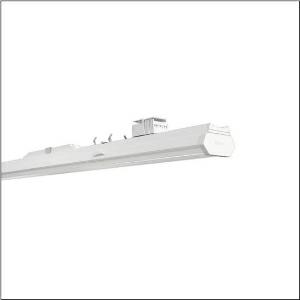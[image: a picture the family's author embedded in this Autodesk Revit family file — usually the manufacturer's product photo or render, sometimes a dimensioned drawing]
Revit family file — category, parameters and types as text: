
# Revit family: licross_r__21_protected_mo_52td1b7n48xg_600d
name_source: partatom
category: Lighting Fixtures
units: mm (PartAtom-declared; Revit-internal decimal feet)

## family parameters
Cut with Voids When Loaded = No
Host = Face
Light Source = No
Part Type = Normal
Room Calculation Point = No
Round Connector Dimension = Use Diameter
Shared = No

## types (1)
- Licross® 21 Protected MO (1 x LED, 8090 lm, 47.9 W, 4000K)
    Apparent Load = 48 VA
    CIE Flux Codes = 54 82 95 97 100
    Color Rendering = 80
    Color Temperature = 4000K
    Default Elevation = 1800 mm
    Description = Licross® 21 Protected MO, luminaire insert, of sheet steel, galvanised, coil coated, white, length: 1.500mm, width: 90mm, height: 103mm, LED rated luminous flux: 8.090lm, light colour: 840, control gear: ON/OFF, with plug, 3-pole, with phase selection, mains connection: 220..240V, AC, 50/60Hz, rated input power: 48W, halogen-free wiring, primary optical cover: cover, of PMMA, light emission: direct distribution, primary light characteristic: symmetric, protection rating (complete): IP54, insulation class (complete): insulation class I (protective earthing), certification: CE, ENEC, VDE, UKCA, protection symbol: D if used in an environment with non-conductive dust loads with corresponding accessories, impact resistance: IK06, permissible ambient temperature for indoor applications: -35..+45°C, corresponds to IFS (International Featured Standards) requirements for safety and quality in the food industry, reducing of maximum allowable ambient temperature of 5°C with ceiling mounting, LABS conformity tested according to VDMA 24364:2018-05, packaging unit: 1 piece
    Height = 92 mm
    Lamp = 1 x LED
    Lamp Light Flux = 8090 lm
    Lamp Power = 47.9 W
    Lamp count = 1
    Length = 1500 mm
    Luminous efficacy = 169 lm/W
    Manufacturer = Siteco
    ModVariant = No
    Model = 52TD1B7N48XG
    Mounting Place = Ceiling
    Mounting Type = Pendant
    Number of Poles = 1
    OnlyDefault = Yes
    Power Factor = 1
    Product Name = Licross® 21 Protected MO
    Product group = luminaire insert
    ProductGroupID = 902
    Protection Class = Protection class I
    Protection Degree = IP 54
    RLX_Detail_Level = 1
    RLX_Emergency_Light_Flux = 0 lm
    RLX_Emergency_Type = 0
    RLX_Emergency_Type_DB = No
    RlxData = <blob elided: 20613 chars, md5=c6c669b1>
    Socket = socket
    Standby Power = 0 W
    System Light Flux = 8090 lm
    System Power = 48 W
    Type Comments = Product without accessories
    Type Image = l_1256148.jpg
    URL = http://relux.com
    VarID = ---
    Voltage = 0 V
    Weight = 0.00 kg
    Width = 88 mm

## geometry (parser evidence)
native form markers: Blend x4, Sweep x12
no freeform markers — native parametric forms only
